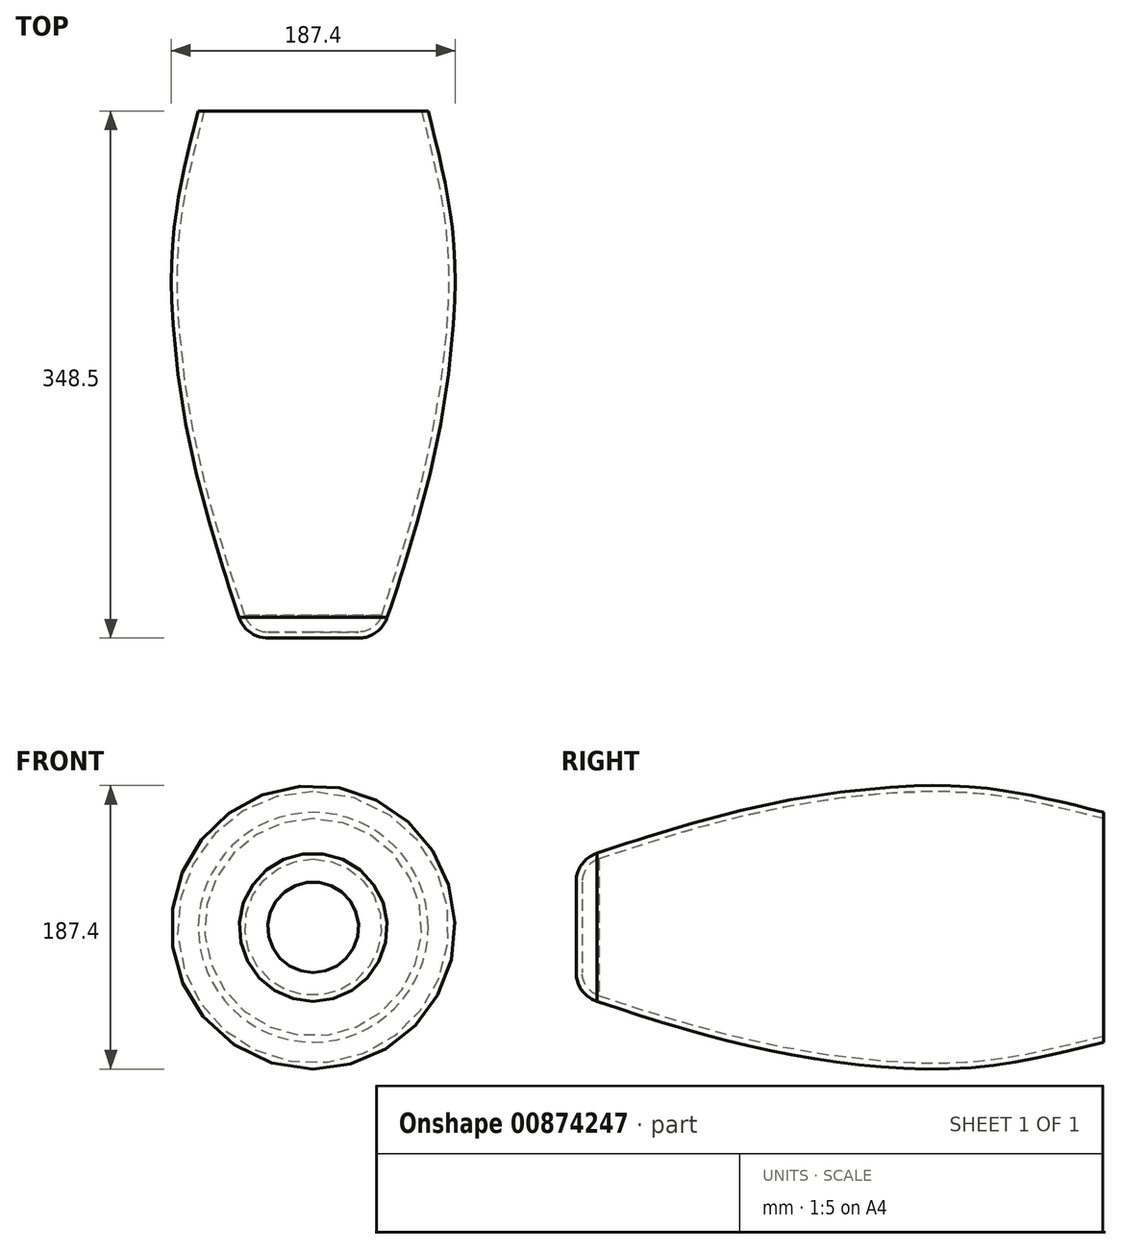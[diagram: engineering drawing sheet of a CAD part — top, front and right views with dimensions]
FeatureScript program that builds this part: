
annotation { "Feature Type Name" : "Feature", "Feature Type Description" : "" }
export const myFeature = defineFeature(function(context is Context, id is Id, definition is map)
    precondition{}
    {
        {
            var Q0;
            Q0=qCreatedBy(makeId("Front.planeOp"),FACE);
            var sketch = newSketch(context, id + "F0", { "sketchPlane" : qUnion([Q0])});
            skCircle(sketch, "E0", {"center": v(0, 0) * mm, "radius": 75.9 * mm});
            skSolve(sketch);
        }
        {
            var Q0;
            Q0=makeQuery(id+"F0.imprint","IMPRINT",FACE,{"disambiguationData":[TD([[makeQuery(id+"F0.imprint","IMPRINT",EDGE,{"derivedFrom":sQuery(id+"F0.wireOp",EDGE,"E0")}),1.0]])]});
            cPlane(context, id + "F1", {"entities" : qUnion([Q0]), "cplaneType" : CPlaneType.OFFSET, "offset" : 77.73 * mm, "width" : 152.4 * mm, "height" : 152.4 * mm});
        }
        {
            var Q0;
            Q0=qCreatedBy(id+"F1.planeOp",FACE);
            var sketch = newSketch(context, id + "F2", { "sketchPlane" : qUnion([Q0])});
            skCircle(sketch, "E1", {"center": v(0, 0) * mm, "radius": 91.88 * mm});
            skSolve(sketch);
        }
        {
            var Q0;
            Q0=qCreatedBy(id+"F1.planeOp",FACE);
            cPlane(context, id + "F3", {"entities" : qUnion([Q0]), "cplaneType" : CPlaneType.OFFSET, "offset" : 80.02 * mm, "width" : 152.4 * mm, "height" : 152.4 * mm});
        }
        {
            var Q0;
            Q0=qCreatedBy(id+"F3.planeOp",FACE);
            var sketch = newSketch(context, id + "F4", { "sketchPlane" : qUnion([Q0])});
            skCircle(sketch, "E2", {"center": v(0, 0) * mm, "radius": 91.24 * mm});
            skSolve(sketch);
        }
        {
            var Q0;
            Q0=qCreatedBy(id+"F3.planeOp",FACE);
            cPlane(context, id + "F5", {"entities" : qUnion([Q0]), "cplaneType" : CPlaneType.OFFSET, "offset" : 104.28 * mm, "width" : 152.4 * mm, "height" : 152.4 * mm});
        }
        {
            var Q0;
            Q0=qCreatedBy(id+"F5.planeOp",FACE);
            var sketch = newSketch(context, id + "F6", { "sketchPlane" : qUnion([Q0])});
            skCircle(sketch, "E3", {"center": v(0, 0) * mm, "radius": 71.53 * mm});
            skSolve(sketch);
        }
        {
            var Q0;
            Q0=qCreatedBy(id+"F5.planeOp",FACE);
            cPlane(context, id + "F7", {"entities" : qUnion([Q0]), "cplaneType" : CPlaneType.OFFSET, "offset" : 86.47 * mm, "width" : 152.4 * mm, "height" : 152.4 * mm});
        }
        {
            var Q0;
            Q0=qCreatedBy(id+"F7.planeOp",FACE);
            var sketch = newSketch(context, id + "F8", { "sketchPlane" : qUnion([Q0])});
            skCircle(sketch, "E4", {"center": v(0, 0) * mm, "radius": 44.34 * mm});
            skSolve(sketch);
        }
        {
            var Q0;
            Q0 = qSketchRegion(id + "F0", true);
            var Q1;
            Q1 = qSketchRegion(id + "F2", true);
            var Q2;
            Q2 = qSketchRegion(id + "F4", true);
            var Q3;
            Q3 = qSketchRegion(id + "F6", true);
            var Q4;
            Q4 = qSketchRegion(id + "F8", true);
            loft(context, id + "F9", {"sheetProfilesArray" : [{ "sheetProfileEntities" : qUnion([Q0]) }, { "sheetProfileEntities" : qUnion([Q1]) }, { "sheetProfileEntities" : qUnion([Q2]) }, { "sheetProfileEntities" : qUnion([Q3]) }, { "sheetProfileEntities" : qUnion([Q4]) }]});
        }
        {
            var Q0;
            Q0=makeQuery(id+"F9.opLoft","MID_CAP_EDGE",EDGE,{"disambiguationData":[OSD([sQuery(id+"F8.wireOp",EDGE,"E4")])],"capPos":4.0});
            fillet(context, id + "F10", {"entities" : qUnion([Q0]), "radius" : 20 * mm, "tangentPropagation" : true, "allowEdgeOverflow" : false});
        }
        {
            var Q0;
            Q0=makeQuery(id+"F9.opLoft","CAP_FACE",FACE,{"disambiguationData":[OSD([makeQuery(id+"F0.imprint","IMPRINT",FACE,{"disambiguationData":[TD([[makeQuery(id+"F0.imprint","IMPRINT",EDGE,{"derivedFrom":sQuery(id+"F0.wireOp",EDGE,"E0")}),1.0]])]})])],"isStart":true});
            shell(context, id + "F11", {"entities" : qUnion([Q0]), "thickness" : 4 * mm});
        }
    });
